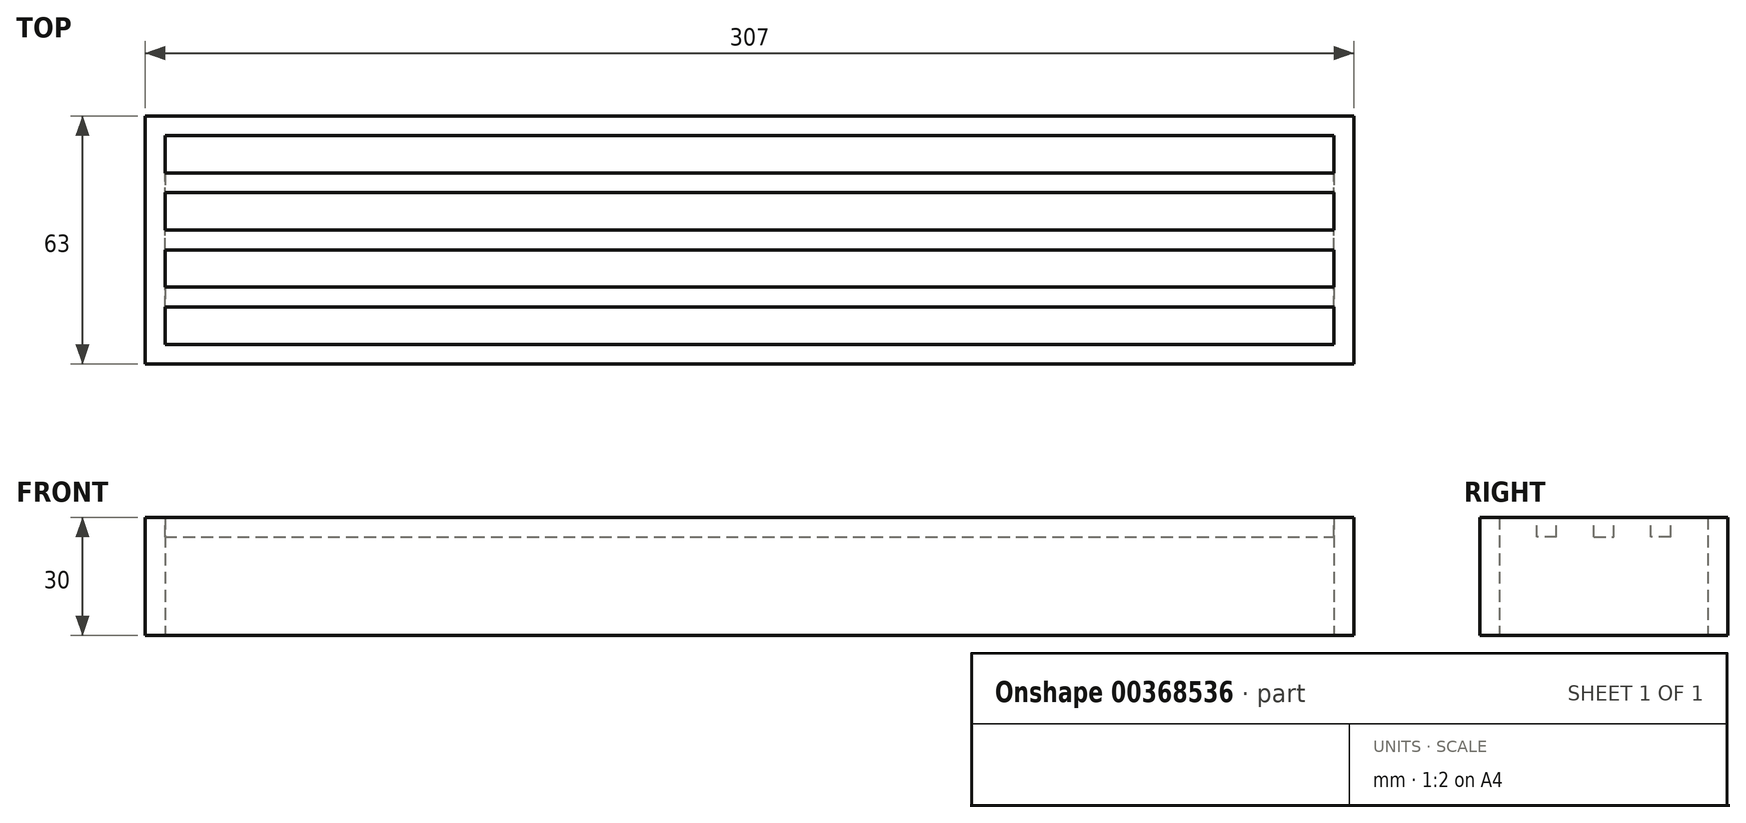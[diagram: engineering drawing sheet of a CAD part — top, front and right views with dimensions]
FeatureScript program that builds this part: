
annotation { "Feature Type Name" : "Feature", "Feature Type Description" : "" }
export const myFeature = defineFeature(function(context is Context, id is Id, definition is map)
    precondition{}
    {
        {
            var Q0;
            Q0=qCreatedBy(makeId("Top.planeOp"),FACE);
            var sketch = newSketch(context, id + "F0", { "sketchPlane" : qUnion([Q0])});
            skLineSegment(sketch, "E0.bottom", {"start": v(153.5, -31.5) * mm, "end": v(-153.5, -31.5) * mm});
            skLineSegment(sketch, "E0.top", {"start": v(153.5, 31.5) * mm, "end": v(-153.5, 31.5) * mm});
            skLineSegment(sketch, "E0.left", {"start": v(153.5, -31.5) * mm, "end": v(153.5, 31.5) * mm});
            skLineSegment(sketch, "E0.right", {"start": v(-153.5, -31.5) * mm, "end": v(-153.5, 31.5) * mm});
            skPoint(sketch, "E0.middle", {"position": v(0, 0) * mm});
            skLineSegment(sketch, "E1.bottom", {"start": v(148.5, -26.5) * mm, "end": v(-148.5, -26.5) * mm});
            skLineSegment(sketch, "E1.top", {"start": v(148.5, 26.5) * mm, "end": v(-148.5, 26.5) * mm});
            skLineSegment(sketch, "E1.left", {"start": v(148.5, -26.5) * mm, "end": v(148.5, 26.5) * mm});
            skLineSegment(sketch, "E1.right", {"start": v(-148.5, -26.5) * mm, "end": v(-148.5, 26.5) * mm});
            skLineSegment(sketch, "E2.bottom", {"start": v(156.5, -34.5) * mm, "end": v(-156.5, -34.5) * mm});
            skLineSegment(sketch, "E2.top", {"start": v(156.5, 34.5) * mm, "end": v(-156.5, 34.5) * mm});
            skLineSegment(sketch, "E2.left", {"start": v(156.5, -34.5) * mm, "end": v(156.5, 34.5) * mm});
            skLineSegment(sketch, "E2.right", {"start": v(-156.5, -34.5) * mm, "end": v(-156.5, 34.5) * mm});
            skSolve(sketch);
        }
        {
            var Q0;
            Q0=qCreatedBy(makeId("Top.planeOp"),FACE);
            cPlane(context, id + "F1", {"entities" : qUnion([Q0]), "cplaneType" : CPlaneType.OFFSET, "offset" : 30 * mm, "width" : 150 * mm, "height" : 150 * mm});
        }
        {
            var Q0;
            Q0=qCreatedBy(id+"F1.planeOp",FACE);
            var sketch = newSketch(context, id + "F2", { "sketchPlane" : qUnion([Q0])});
            skLineSegment(sketch, "E3.bottom", {"start": v(-148.5, 17) * mm, "end": v(148.5, 17) * mm});
            skLineSegment(sketch, "E4.top", {"start": v(148.5, 12) * mm, "end": v(-148.5, 12) * mm});
            skLineSegment(sketch, "E5.left", {"start": v(-148.5, 17) * mm, "end": v(-148.5, 12) * mm});
            skLineSegment(sketch, "E5.right", {"start": v(148.5, 17) * mm, "end": v(148.5, 12) * mm});
            skLineSegment(sketch, "E6.bottom", {"start": v(-148.5, -12) * mm, "end": v(148.5, -12) * mm});
            skLineSegment(sketch, "E6.top", {"start": v(-148.5, -17) * mm, "end": v(148.5, -17) * mm});
            skLineSegment(sketch, "E6.left", {"start": v(-148.5, -12) * mm, "end": v(-148.5, -17) * mm});
            skLineSegment(sketch, "E6.right", {"start": v(148.5, -12) * mm, "end": v(148.5, -17) * mm});
            skLineSegment(sketch, "E7.bottom", {"start": v(148.5, -2.5) * mm, "end": v(-148.5, -2.5) * mm});
            skLineSegment(sketch, "E7.top", {"start": v(148.5, 2.5) * mm, "end": v(-148.5, 2.5) * mm});
            skLineSegment(sketch, "E7.left", {"start": v(148.5, -2.5) * mm, "end": v(148.5, 2.5) * mm});
            skLineSegment(sketch, "E7.right", {"start": v(-148.5, -2.5) * mm, "end": v(-148.5, 2.5) * mm});
            skPoint(sketch, "E7.middle", {"position": v(0, 0) * mm});
            skSolve(sketch);
        }
        {
            var Q0;
            Q0=makeQuery(id+"F0.imprint","IMPRINT",FACE,{"disambiguationData":[TD([[makeQuery(id+"F0.imprint","IMPRINT",EDGE,{"derivedFrom":sQuery(id+"F0.wireOp",EDGE,"E0.bottom")}),-1.0]])]});
            extrude(context, id + "F3", {"entities" : qUnion([Q0]), "depth" : 30 * mm});
        }
        {
            var Q0;
            Q0=makeQuery(id+"F2.imprint","IMPRINT",FACE,{"disambiguationData":[TD([[makeQuery(id+"F2.imprint","IMPRINT",EDGE,{"derivedFrom":sQuery(id+"F2.wireOp",EDGE,"E3.bottom")}),-1.0]])]});
            var Q1;
            Q1=makeQuery(id+"F2.imprint","IMPRINT",FACE,{"disambiguationData":[TD([[makeQuery(id+"F2.imprint","IMPRINT",EDGE,{"derivedFrom":sQuery(id+"F2.wireOp",EDGE,"E7.bottom")}),-1.0]])]});
            var Q2;
            Q2=makeQuery(id+"F2.imprint","IMPRINT",FACE,{"disambiguationData":[TD([[makeQuery(id+"F2.imprint","IMPRINT",EDGE,{"derivedFrom":sQuery(id+"F2.wireOp",EDGE,"E6.bottom")}),-1.0]])]});
            extrude(context, id + "F4", {"entities" : qUnion([Q0, Q1, Q2]), "operationType" : NewBodyOperationType.ADD, "oppositeDirection" : true, "depth" : 5 * mm});
        }
    });
